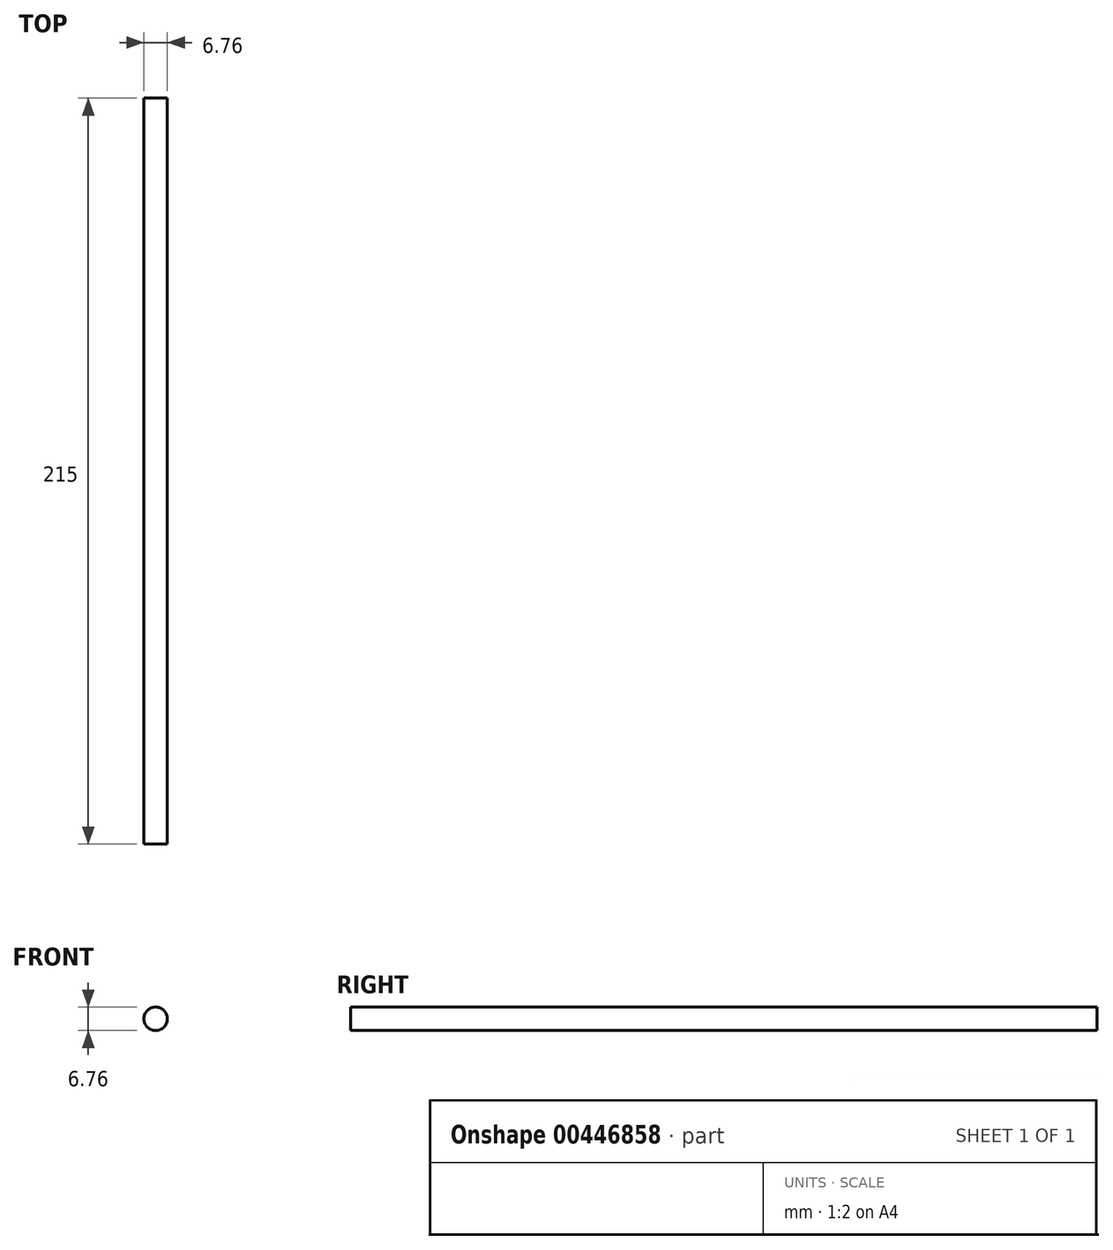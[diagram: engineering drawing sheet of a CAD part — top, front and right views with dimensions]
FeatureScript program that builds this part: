
annotation { "Feature Type Name" : "Feature", "Feature Type Description" : "" }
export const myFeature = defineFeature(function(context is Context, id is Id, definition is map)
    precondition{}
    {
        {
            var Q0;
            Q0=qCreatedBy(makeId("Front.planeOp"),FACE);
            var sketch = newSketch(context, id + "F0", { "sketchPlane" : qUnion([Q0])});
            skCircle(sketch, "E0", {"center": v(0, 0) * mm, "radius": 3.38 * mm});
            skSolve(sketch);
        }
        {
            var Q0;
            Q0=makeQuery(id+"F0.imprint","IMPRINT",FACE,{"disambiguationData":[TD([[makeQuery(id+"F0.imprint","IMPRINT",EDGE,{"derivedFrom":sQuery(id+"F0.wireOp",EDGE,"E0")}),1.0]])]});
            extrude(context, id + "F1", {"entities" : qUnion([Q0]), "depth" : 215 * mm});
        }
    });
